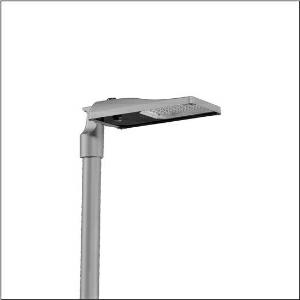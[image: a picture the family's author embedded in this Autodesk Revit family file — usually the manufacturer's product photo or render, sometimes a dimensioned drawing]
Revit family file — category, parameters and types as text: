
# Revit family: streetlight_sl_31_mini___st1_0a_5xh2d3at08ja_abb8
name_source: partatom
category: Lighting Fixtures
units: mm (PartAtom-declared; Revit-internal decimal feet)

## family parameters
Cut with Voids When Loaded = No
Host = Face
Light Source = No
Part Type = Normal
Room Calculation Point = No
Round Connector Dimension = Use Diameter
Shared = No

## types (1)
- --- (1 x LED, 12270 lm, 82.5 W, 3000K)
    Apparent Load = 83 VA
    CIE Flux Codes = 40 73 97 100 100
    Color Rendering = 70
    Color Temperature = 3000K
    Default Elevation = 1800 mm
    Description = Streetlight SL 31 mini D4i mast luminaire for post-top, side-entry; light control with lens of PMMA; light distribution: ST1.0a, direct asymmetric distribution, for standard-compliant lighting for roads and squares; LED: luminous flux: 12.270lm, light colour: 730, colour temperature: 3000K; luminous efficacy: 148,7lm/W; control: pre-setting: logarithmic dimming characteristic, flexible luminous flux parameterisation, time-dependent luminous flux control, constant luminous flux control, power reduction, intelligent temperature release in ECG and LED module, overheat protection; luminaire housing, of diecast aluminium, SITECO metallic grey (DB 702S), corrosivity category C5 high according to DIN EN ISO 12944; cover of toughened safety glass, transparent, mast flange of diecast aluminium, SITECO metallic grey (DB 702S), spigot size: 76/60mm, mast flange included unmounted; cable length: 10,5m, connection cable pre-assembled; mains connection: 220..240V, AC, 50/60Hz; power consumption (at start of service life): 82,5W / (at end of service life): 90,1W / (with reduced operation 50%): 36,8W; protection rating (complete): IP66; insulation class (complete): insulation class II (safety insulation); impact resistance: IK09; certification: CE, ENEC, ENEC+, VDE, UKCA, ZD4i; permissible operating ambient temperature for outdoor applications: -40..+50°C; packaging unit: 1 piece

Light Distribution: ST1.0a
    Height = 76 mm
    Lamp = 1 x LED
    Lamp Light Flux = 12270 lm
    Lamp Power = 82.5 W
    Lamp count = 1
    Length = 547 mm
    Luminous efficacy = 149 lm/W
    Manufacturer = Siteco
    ModVariant = No
    Model = 5XH2D3AT08JA
    Number of Poles = 1
    OnlyDefault = Yes
    Power Factor = 1
    Product Name = Streetlight SL 31 mini | ST1.0a
    Product group = mast luminaire | pylon top
    ProductGroupID = 6100
    Protection Class = Protection class II
    Protection Degree = IP 66
    RLX_Detail_Level = 1
    RLX_Emergency_Light_Flux = 0 lm
    RLX_Emergency_Type = 0
    RLX_Emergency_Type_DB = No
    RlxData = <blob elided: 39709 chars, md5=96028bed>
    Socket = socket
    Standby Power = 0 W
    System Light Flux = 12270 lm
    System Power = 83 W
    Type Comments = factory setting: luminous flux: 100 % | dim-lin: 254 | 870 mA
    Type Image = l_1300332.jpg
    URL = http://relux.com
    VarID = @adj_057595
    Voltage = 0 V
    Weight = 0.00 kg
    Width = 265 mm

## geometry (parser evidence)
native form markers: Blend x4, Sweep x9
no freeform markers — native parametric forms only
